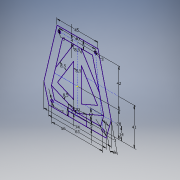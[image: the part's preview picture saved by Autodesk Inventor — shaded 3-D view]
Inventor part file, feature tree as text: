
AUTODESK INVENTOR PART (.ipt)
format: ipt  version: 2019 (Build 230136000, 136)  size: 108,032 bytes
history: native  units: mm (DEFAULTED — no unit token found)
features: sketch x1
ambient origin geometry x8: Origin, YZ Plane, XZ Plane, XY Plane, X Axis, Y Axis, Z Axis, Center Point
feature tree (1):
  sketch  "Sketch1"  dims[d0=40.0mm d1=42.0mm d2=28.0mm d3=56.0mm d5=3.0mm d6=3.0mm d7=3.0mm d8=3.0mm d9=45.0mm d10=74.0mm d11=63.0mm d12=2.5mm d13=8.0mm d14=9.0mm d15=4.0mm d16=8.0mm d17=8.0mm d18=12.0mm d19=8.5mm d20=8.5mm d21=8.5mm d22=14.0mm d23=41.0mm d24=8.5mm d25=1.5mm d26=20.0mm d27=5.0mm]
